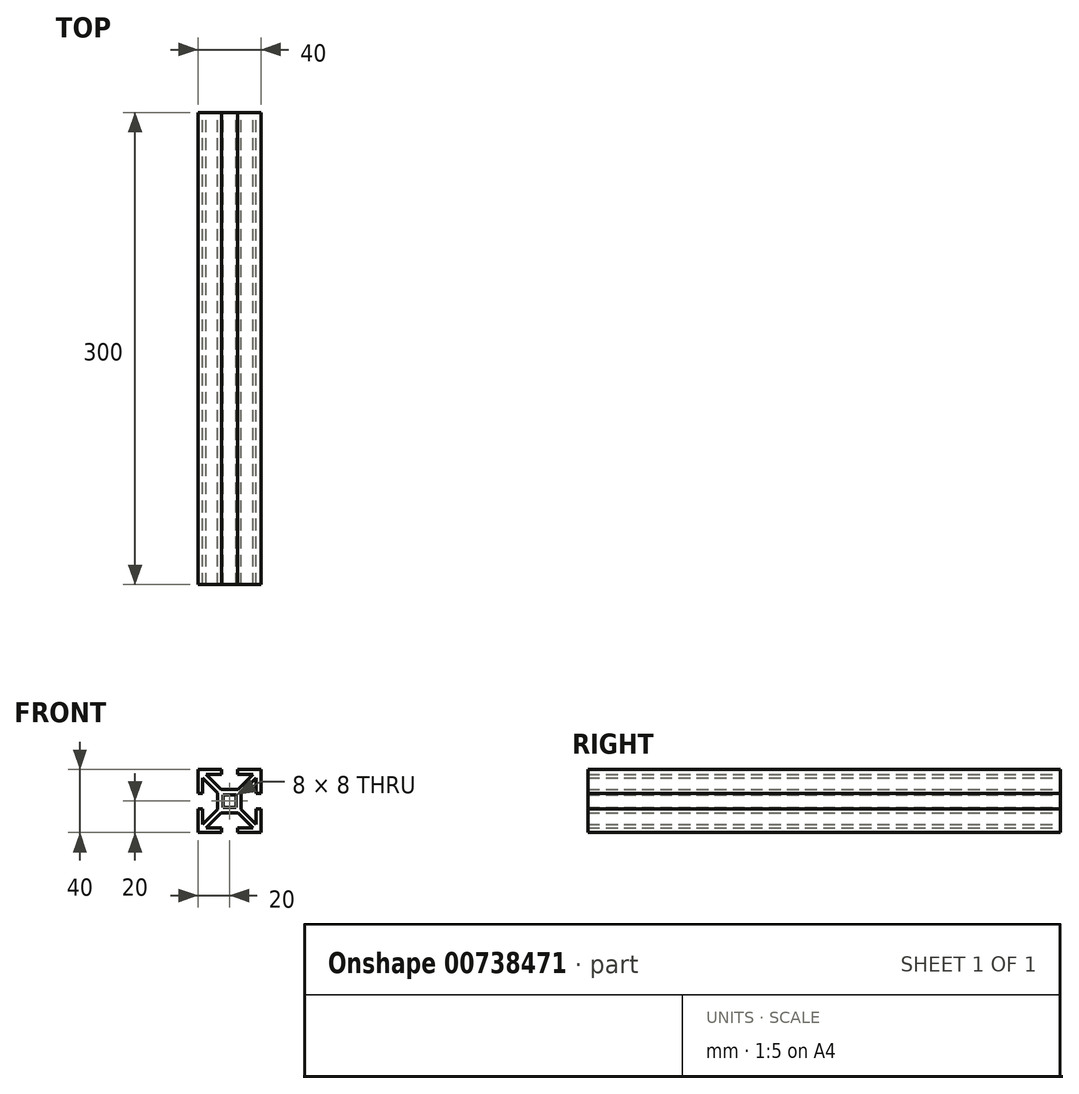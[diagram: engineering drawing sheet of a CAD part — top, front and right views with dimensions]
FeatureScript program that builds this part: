
annotation { "Feature Type Name" : "Feature", "Feature Type Description" : "" }
export const myFeature = defineFeature(function(context is Context, id is Id, definition is map)
    precondition{}
    {
        {
            var Q0;
            Q0=qCreatedBy(makeId("Front.planeOp"),FACE);
            var sketch = newSketch(context, id + "F0", { "sketchPlane" : qUnion([Q0])});
            skPoint(sketch, "E0.middle", {"position": v(0, 0) * mm});
            skLineSegment(sketch, "E1.bottom", {"start": v(20, 20) * mm, "end": v(-20, 20) * mm});
            skLineSegment(sketch, "E1.top", {"start": v(20, -20) * mm, "end": v(-20, -20) * mm});
            skLineSegment(sketch, "E1.left", {"start": v(20, 20) * mm, "end": v(20, -20) * mm});
            skLineSegment(sketch, "E1.right", {"start": v(-20, 20) * mm, "end": v(-20, -20) * mm});
            skLineSegment(sketch, "E2.bottom", {"start": v(4, 4) * mm, "end": v(-4, 4) * mm});
            skLineSegment(sketch, "E2.top", {"start": v(4, -4) * mm, "end": v(-4, -4) * mm});
            skLineSegment(sketch, "E2.left", {"start": v(4, 4) * mm, "end": v(4, -4) * mm});
            skLineSegment(sketch, "E2.right", {"start": v(-4, 4) * mm, "end": v(-4, -4) * mm});
            skLineSegment(sketch, "E3.bottom", {"start": v(7.5, -7.5) * mm, "end": v(-7.5, -7.5) * mm});
            skLineSegment(sketch, "E3.top", {"start": v(7.5, 7.5) * mm, "end": v(-7.5, 7.5) * mm});
            skLineSegment(sketch, "E3.left", {"start": v(7.5, -7.5) * mm, "end": v(7.5, 7.5) * mm});
            skLineSegment(sketch, "E3.right", {"start": v(-7.5, -7.5) * mm, "end": v(-7.5, 7.5) * mm});
            skLineSegment(sketch, "E4", {"start": v(-5, 20) * mm, "end": v(-5, -20) * mm, "construction": true});
            skLineSegment(sketch, "E5", {"start": v(5, -20) * mm, "end": v(5, 20) * mm, "construction": true});
            skLineSegment(sketch, "E6", {"start": v(-20, 5) * mm, "end": v(20, 5) * mm, "construction": true});
            skLineSegment(sketch, "E7", {"start": v(-20, -5) * mm, "end": v(20, -5) * mm, "construction": true});
            skLineSegment(sketch, "E8.bottom", {"start": v(17, 17) * mm, "end": v(-17, 17) * mm});
            skLineSegment(sketch, "E8.top", {"start": v(17, -17) * mm, "end": v(-17, -17) * mm});
            skLineSegment(sketch, "E8.left", {"start": v(17, 17) * mm, "end": v(17, -17) * mm});
            skLineSegment(sketch, "E8.right", {"start": v(-17, 17) * mm, "end": v(-17, -17) * mm});
            skLineSegment(sketch, "E9", {"start": v(0, 0) * mm, "end": v(20, 20) * mm, "construction": true});
            skLineSegment(sketch, "E10", {"start": v(0, 0) * mm, "end": v(20, -20) * mm, "construction": true});
            skLineSegment(sketch, "E11", {"start": v(0, 0) * mm, "end": v(-20, -20) * mm, "construction": true});
            skLineSegment(sketch, "E12", {"start": v(0, 0) * mm, "end": v(-20, 20) * mm, "construction": true});
            skLineSegment(sketch, "E13", {"start": v(5.38, 7.5) * mm, "end": v(14.88, 17) * mm});
            skLineSegment(sketch, "E14", {"start": v(7.5, 5.38) * mm, "end": v(17, 14.88) * mm});
            skLineSegment(sketch, "E15", {"start": v(7.5, -5.38) * mm, "end": v(17, -14.88) * mm});
            skLineSegment(sketch, "E16", {"start": v(5.38, -7.5) * mm, "end": v(14.88, -17) * mm});
            skLineSegment(sketch, "E17", {"start": v(-7.5, -5.38) * mm, "end": v(-17, -14.88) * mm});
            skLineSegment(sketch, "E18", {"start": v(-14.88, -17) * mm, "end": v(-5.38, -7.5) * mm});
            skLineSegment(sketch, "E19", {"start": v(-5.38, 7.5) * mm, "end": v(-14.88, 17) * mm});
            skLineSegment(sketch, "E20", {"start": v(-7.5, 5.38) * mm, "end": v(-17, 14.88) * mm});
            skLineSegment(sketch, "E21", {"start": v(-5, 20) * mm, "end": v(-5, 17) * mm});
            skLineSegment(sketch, "E22", {"start": v(5, 20) * mm, "end": v(5, 17) * mm});
            skLineSegment(sketch, "E23", {"start": v(17, 5) * mm, "end": v(20, 5) * mm});
            skLineSegment(sketch, "E24", {"start": v(17, -5) * mm, "end": v(20, -5) * mm});
            skLineSegment(sketch, "E25", {"start": v(5, -17) * mm, "end": v(5, -20) * mm});
            skLineSegment(sketch, "E26", {"start": v(-5, -17) * mm, "end": v(-5, -20) * mm});
            skLineSegment(sketch, "E27", {"start": v(-17, -5) * mm, "end": v(-20, -5) * mm});
            skLineSegment(sketch, "E28", {"start": v(-17, 5) * mm, "end": v(-20, 5) * mm});
            skSolve(sketch);
        }
        {
            var Q0;
            {var subQ2=sQuery(id+"F0.wireOp",EDGE,"E21");Q0=makeQuery(id+"F0.imprint","IMPRINT",FACE,{"disambiguationData":[TD([[makeQuery(id+"F0.imprint","IMPRINT",EDGE,{"derivedFrom":subQ2}),-1.0]])]});}
            var Q1;
            {var subQ4=sQuery(id+"F0.wireOp",EDGE,"E26");Q1=makeQuery(id+"F0.imprint","IMPRINT",FACE,{"disambiguationData":[TD([[makeQuery(id+"F0.imprint","IMPRINT",EDGE,{"derivedFrom":subQ4}),-1.0]])]});}
            var Q2;
            {var subQ8=sQuery(id+"F0.wireOp",EDGE,"E24");Q2=makeQuery(id+"F0.imprint","IMPRINT",FACE,{"disambiguationData":[TD([[makeQuery(id+"F0.imprint","IMPRINT",EDGE,{"derivedFrom":subQ8}),-1.0]])]});}
            var Q3;
            {var subQ2=sQuery(id+"F0.wireOp",EDGE,"E22");Q3=makeQuery(id+"F0.imprint","IMPRINT",FACE,{"disambiguationData":[TD([[makeQuery(id+"F0.imprint","IMPRINT",EDGE,{"derivedFrom":subQ2}),1.0]])]});}
            var Q4;
            {var subQ4=sQuery(id+"F0.wireOp",EDGE,"E13");Q4=makeQuery(id+"F0.imprint","IMPRINT",FACE,{"disambiguationData":[TD([[makeQuery(id+"F0.imprint","IMPRINT",EDGE,{"derivedFrom":subQ4}),-1.0]])]});}
            var Q5;
            {var subQ4=sQuery(id+"F0.wireOp",EDGE,"E19");Q5=makeQuery(id+"F0.imprint","IMPRINT",FACE,{"disambiguationData":[TD([[makeQuery(id+"F0.imprint","IMPRINT",EDGE,{"derivedFrom":subQ4}),1.0]])]});}
            var Q6;
            {var subQ3=sQuery(id+"F0.wireOp",EDGE,"E17");Q6=makeQuery(id+"F0.imprint","IMPRINT",FACE,{"disambiguationData":[TD([[makeQuery(id+"F0.imprint","IMPRINT",EDGE,{"derivedFrom":subQ3}),1.0]])]});}
            var Q7;
            {var subQ7=sQuery(id+"F0.wireOp",EDGE,"E15");Q7=makeQuery(id+"F0.imprint","IMPRINT",FACE,{"disambiguationData":[TD([[makeQuery(id+"F0.imprint","IMPRINT",EDGE,{"derivedFrom":subQ7}),-1.0]])]});}
            var Q8;
            Q8=makeQuery(id+"F0.imprint","IMPRINT",FACE,{"disambiguationData":[TD([[makeQuery(id+"F0.imprint","IMPRINT",EDGE,{"derivedFrom":sQuery(id+"F0.wireOp",EDGE,"E2.bottom")}),-1.0]])]});
            extrude(context, id + "F1", {"entities" : qUnion([Q0, Q1, Q2, Q3, Q4, Q5, Q6, Q7, Q8]), "endBound" : BoundingType.SYMMETRIC, "depth" : 300 * mm, "offsetDistance" : 25 * mm});
        }
    });
